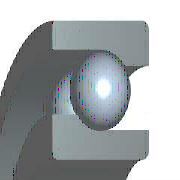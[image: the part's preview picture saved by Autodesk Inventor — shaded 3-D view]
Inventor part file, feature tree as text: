
AUTODESK INVENTOR PART (.ipt)
format: ipt  version: 2018 (Build 220112000, 112)  size: 294,912 bytes
history: native  units: mm
features: revolve x2, fillet x2, pattern_circular x1
ambient origin geometry x8: Origin, YZ Plane, XZ Plane, XY Plane, X Axis, Y Axis, Z Axis, Center Point
bodies: Solid1 (feature_tree)
feature tree (5):
  revolve  "旋转1"  [1 undecoded]
  fillet  "圆角1"  Radius=32.0mm
  fillet  "圆角2"  Radius=10.0mm
  revolve  "旋转2"  [1 undecoded]
  pattern_circular  "环形阵列1"  Angle=90.0deg  [1 undecoded]
note: 3 required parameter values undecoded (feature->parameter linkage not recoverable at this tier; creation-order binding heuristic only, values carry confidence <= 0.55)